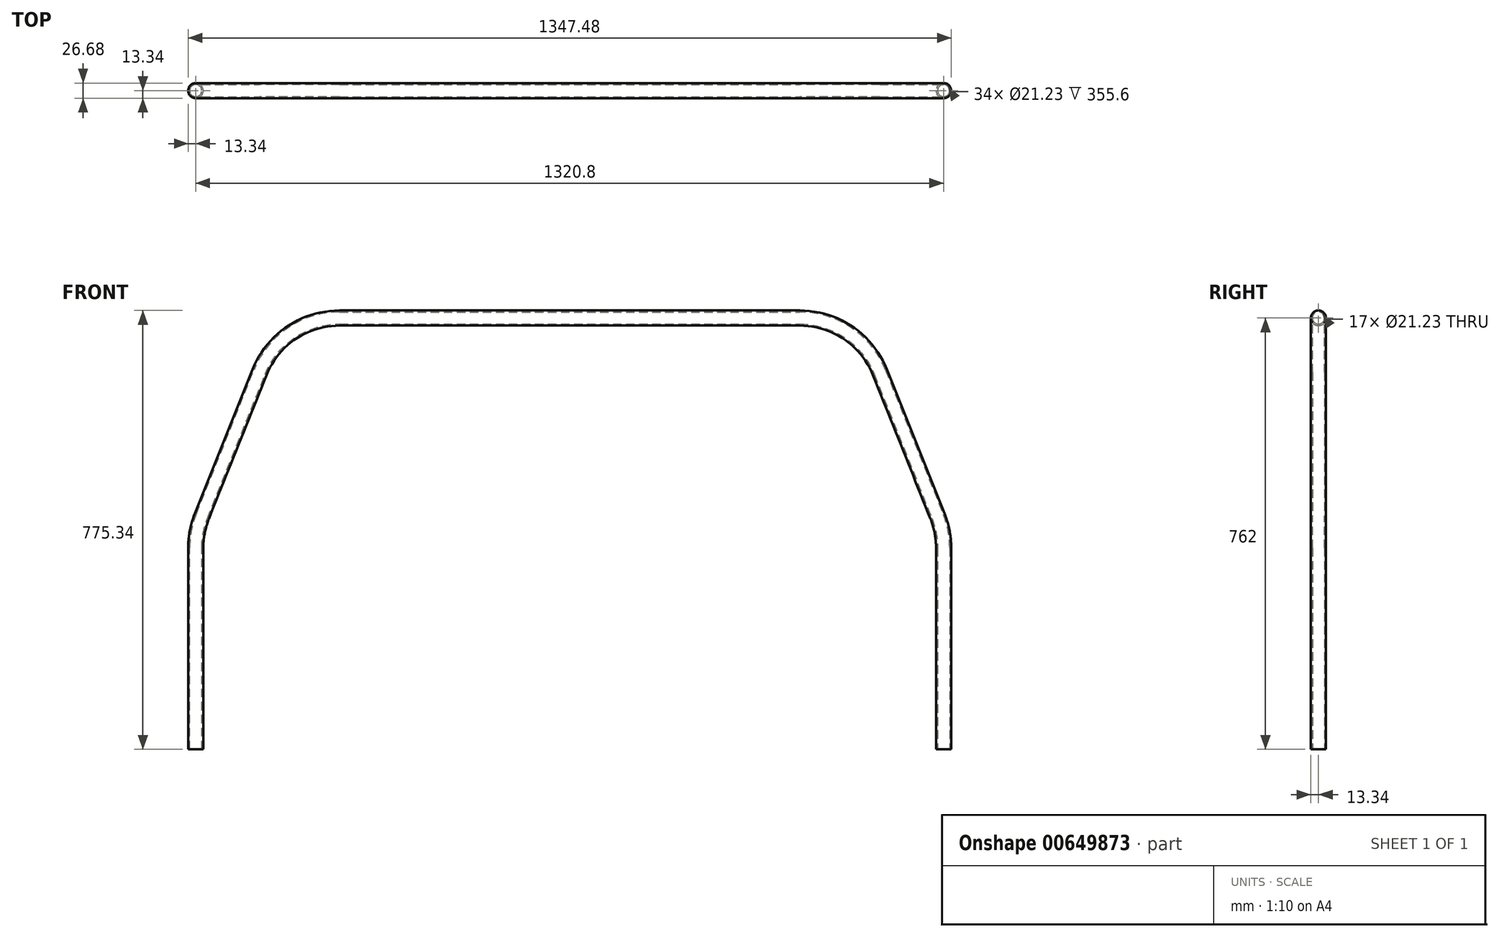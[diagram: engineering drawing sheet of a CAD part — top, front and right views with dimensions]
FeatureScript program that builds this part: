
annotation { "Feature Type Name" : "Feature", "Feature Type Description" : "" }
export const myFeature = defineFeature(function(context is Context, id is Id, definition is map)
    precondition{}
    {
        {
            var Q0;
            Q0=qCreatedBy(makeId("Front.planeOp"),FACE);
            var sketch = newSketch(context, id + "F0", { "sketchPlane" : qUnion([Q0])});
            skLineSegment(sketch, "E0", {"start": v(0, 0) * mm, "end": v(0, 762) * mm, "construction": true});
            skLineSegment(sketch, "E1", {"start": v(0, 762) * mm, "end": v(-406.4, 762) * mm});
            skLineSegment(sketch, "E2", {"start": v(-547.9, 666.2) * mm, "end": v(-649.5, 412.2) * mm});
            skLineSegment(sketch, "E3", {"start": v(-660.4, 355.6) * mm, "end": v(-660.4, 0) * mm});
            skPoint(sketch, "E4.visualSharp", {"position": v(-660.4, 384.95) * mm});
            skArc(sketch, "E4.filletArc", {"start": v(-649.5, 412.2) * mm, "mid": v(-657.65, 384.42) * mm, "end": v(-660.4, 355.6) * mm});
            skPoint(sketch, "E5.visualSharp", {"position": v(-509.58, 762) * mm});
            skArc(sketch, "E5.filletArc", {"start": v(-406.4, 762) * mm, "mid": v(-491.84, 735.8) * mm, "end": v(-547.9, 666.2) * mm});
            skArc(sketch, "E6.MirrorCS", {"start": v(649.5, 412.2) * mm, "mid": v(657.65, 384.42) * mm, "end": v(660.4, 355.6) * mm});
            skPoint(sketch, "E7.MirrorP", {"position": v(660.4, 384.95) * mm});
            skPoint(sketch, "E8.MirrorP", {"position": v(509.58, 762) * mm});
            skLineSegment(sketch, "E9.MirrorCS", {"start": v(660.4, 355.6) * mm, "end": v(660.4, 0) * mm});
            skLineSegment(sketch, "E10.MirrorCS", {"start": v(547.9, 666.2) * mm, "end": v(649.5, 412.2) * mm});
            skLineSegment(sketch, "E11.MirrorCS", {"start": v(0, 762) * mm, "end": v(406.4, 762) * mm});
            skArc(sketch, "E12.MirrorCS", {"start": v(406.4, 762) * mm, "mid": v(491.84, 735.8) * mm, "end": v(547.9, 666.2) * mm});
            skSolve(sketch);
        }
        {
            var Q0;
            Q0=qCreatedBy(makeId("Top.planeOp"),FACE);
            var sketch = newSketch(context, id + "F1", { "sketchPlane" : qUnion([Q0])});
            skPoint(sketch, "E13.0", {"position": v(-660.4, 0) * mm});
            skCircle(sketch, "E14", {"center": v(-660.4, 0) * mm, "radius": 13.34 * mm});
            skCircle(sketch, "E15", {"center": v(-660.4, 0) * mm, "radius": 10.62 * mm});
            skSolve(sketch);
        }
        {
            var Q0;
            Q0 = qSketchRegion(id + "F1", true);
            var Q1;
            Q1 = qConstructionFilter(qBodyType(qCreatedBy(id + "F0" ,EDGE), BodyType.WIRE), ConstructionObject.NO);
            sweep(context, id + "F2", {"profiles" : qUnion([Q0]), "path" : qUnion([Q1])});
        }
    });
